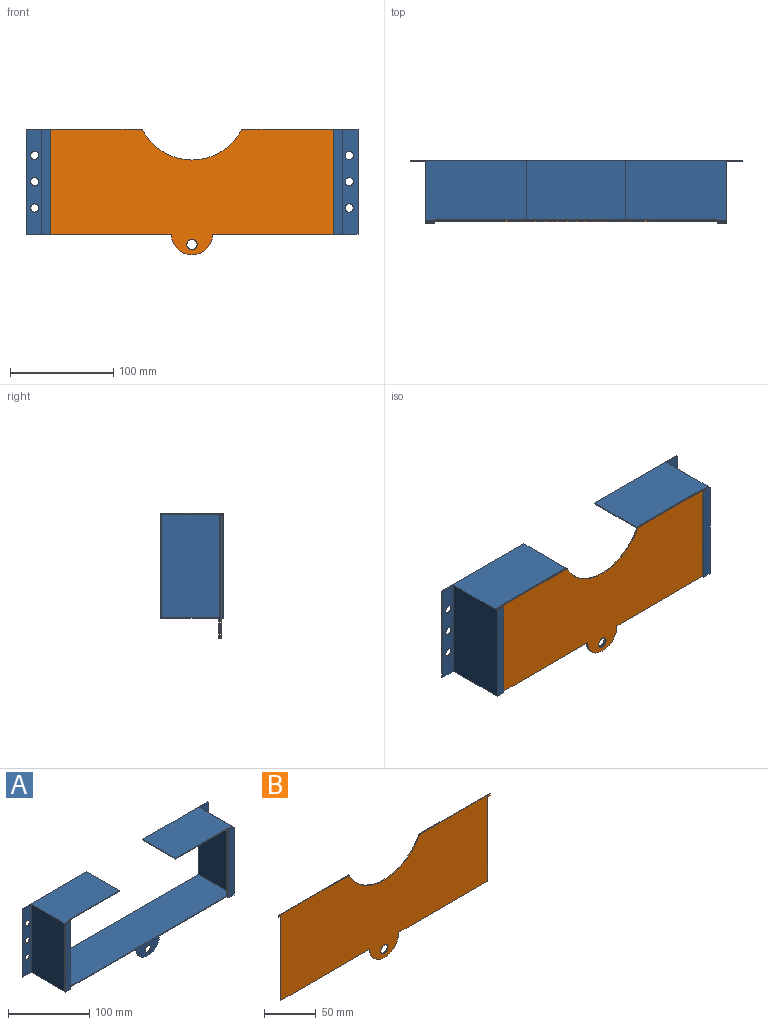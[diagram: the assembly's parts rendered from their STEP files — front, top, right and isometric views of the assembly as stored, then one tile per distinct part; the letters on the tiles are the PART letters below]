
ASSEMBLY  parts=2 mates=1
PART A: 47 faces, bbox 322x61x122 mm
  f0: plane 102x8mm, normal (0,1,0), area 813mm2, adj f4,f5,f12,f13,f42,f43
  f1: plane 100x57.5mm, normal (1,0,0), area 5750mm2, adj f8,f9,f33,f45
  f2: plane 102x60mm, normal (-1,0,0), area 6120mm2, adj f3,f11,f12,f13
  f3: plane 102x9mm, normal (0,-1,0), area 918mm2, adj f2,f4,f12,f13
  f4: plane 102x1mm, normal (1,0,0), area 102mm2, adj f0,f3,f12,f13
  f5: plane 101x1.5mm, normal (1,0,0), area 151.5mm2, adj f0,f6,f12,f43
  f6: plane 102x8mm, normal (0,-1,0), area 813mm2, adj f5,f7,f12,f13,f42,f43
  f7: plane 102x1mm, normal (1,0,0), area 102mm2, adj f6,f8,f12,f13,f17,f44
  f8: plane 100x8mm, normal (0,1,0), area 800mm2, adj f1,f7,f33,f45
  f9: plane 322x102mm, normal (0,1,0), area 3445.6mm2, adj f1,f10,f12,f13,f14,f15,f16,f21
  f10: plane 102x1mm, normal (-1,0,0), area 102mm2, adj f9,f11,f12,f13
  f11: plane 102x15mm, normal (0,-1,0), area 1379.2mm2, adj f2,f10,f12,f13,f14,f15,f16
  f12: plane 112.57x61mm, normal (0,0,1), area 5645mm2, adj f0,f2,f3,f4,f5,f6,f7,f9
  f13: plane 322x61mm, normal (0,0,-1), area 16828mm2, adj f0,f2,f3,f4,f6,f7,f9,f10
  f14: cylinder r=4mm len=8mm, axis (0,1,0), area 25.1mm2, adj f9,f11
  f15: cylinder r=4mm len=8mm, axis (0,1,0), area 25.1mm2, adj f9,f11
  f16: cylinder r=4mm len=8mm, axis (0,1,0), area 25.1mm2, adj f9,f11
  f17: plane 274x21mm, normal (0,-1,0), area 823.8mm2, adj f7,f13,f24,f33,f34,f35
  f18: plane 100x8mm, normal (0,1,0), area 800mm2, adj f21,f24,f33,f40
  f19: plane 102x8mm, normal (0,-1,0), area 813mm2, adj f13,f20,f24,f29,f37,f38
  f20: plane 101x1.5mm, normal (-1,0,0), area 151.5mm2, adj f19,f25,f29,f38
  f21: plane 100x57.5mm, normal (-1,0,0), area 5750mm2, adj f9,f18,f33,f40
  f22: plane 102x15mm, normal (0,-1,0), area 1379.2mm2, adj f13,f23,f28,f29,f30,f31,f32
  f23: plane 102x1mm, normal (1,0,0), area 102mm2, adj f9,f13,f22,f29
  f24: plane 102x1mm, normal (-1,0,0), area 102mm2, adj f13,f17,f18,f19,f29,f39
  f25: plane 102x8mm, normal (0,1,0), area 813mm2, adj f13,f20,f26,f29,f37,f38
  f26: plane 102x1mm, normal (-1,0,0), area 102mm2, adj f13,f25,f27,f29
  f27: plane 102x9mm, normal (0,-1,0), area 918mm2, adj f13,f26,f28,f29
  f28: plane 102x60mm, normal (1,0,0), area 6120mm2, adj f13,f22,f27,f29
  f29: plane 112.62x61mm, normal (0,0,1), area 5647.4mm2, adj f9,f19,f20,f22,f23,f24,f25,f26
  f30: cylinder r=4mm len=8mm, axis (0,1,0), area 25.1mm2, adj f9,f22
  f31: cylinder r=4mm len=8mm, axis (0,1,0), area 25.1mm2, adj f9,f22
  f32: cylinder r=4mm len=8mm, axis (0,1,0), area 25.1mm2, adj f9,f22
  f33: plane 290x57.5mm, normal (0,0,1), area 16675mm2, adj f1,f8,f9,f17,f18,f21
  f34: cylinder r=5mm len=10mm, axis (0,-1,0), area 31.4mm2, adj f17,f36
  f35: cylinder r=20mm len=40mm, axis (0,-1,0), area 62.8mm2, adj f13,f17,f36
  f36: plane 40x20mm, normal (0,1,0), area 549.8mm2, adj f13,f34,f35
  f37: plane 1.5x1mm, normal (-1,0,0), area 1.5mm2, adj f13,f19,f25,f38
  f38: plane 3x1.5mm, normal (0,0,1), area 4.5mm2, adj f19,f20,f25,f37
  f39: plane 88.62x1mm, normal (0,-1,0), area 88.6mm2, adj f24,f29,f40,f41
  f40: plane 96.62x57.5mm, normal (0,0,-1), area 5555.4mm2, adj f9,f18,f21,f39,f41
  f41: plane 57.5x1mm, normal (-1,0,0), area 57.5mm2, adj f9,f29,f39,f40
  f42: plane 1.5x1mm, normal (1,0,0), area 1.5mm2, adj f0,f6,f13,f43
  f43: plane 3x1.5mm, normal (0,0,1), area 4.5mm2, adj f0,f5,f6,f42
  f44: plane 88.57x1mm, normal (0,-1,0), area 88.6mm2, adj f7,f12,f45,f46
  f45: plane 96.57x57.5mm, normal (0,0,-1), area 5553mm2, adj f1,f8,f9,f44,f46
  f46: plane 57.5x1mm, normal (1,0,0), area 57.5mm2, adj f9,f12,f44,f45
PART B: 15 faces, bbox 290x1x122 mm
  f0: plane 96.63x1mm, normal (0,0,1), area 96.6mm2, adj f2,f3,f8,f14
  f1: plane 96.63x1mm, normal (0,0,1), area 96.6mm2, adj f2,f3,f7,f14
  f2: plane 290x122mm, normal (0,-1,0), area 27453.3mm2, adj f0,f1,f4,f5,f6,f7,f8,f9
  f3: plane 290x122mm, normal (0,1,0), area 27453.3mm2, adj f0,f1,f4,f5,f6,f7,f8,f9
  f4: plane 122x1mm, normal (0,0,-1), area 122mm2, adj f2,f3,f5,f13
  f5: plane 100x1mm, normal (1,0,0), area 100mm2, adj f2,f3,f4,f6
  f6: plane 3x1mm, normal (0,0,-1), area 3mm2, adj f2,f3,f5,f7
  f7: plane 2x1mm, normal (1,0,0), area 2mm2, adj f1,f2,f3,f6
  f8: plane 2x1mm, normal (-1,0,0), area 2mm2, adj f0,f2,f3,f9
  f9: plane 3x1mm, normal (0,0,-1), area 3mm2, adj f2,f3,f8,f10
  f10: plane 100x1mm, normal (-1,0,0), area 100mm2, adj f2,f3,f9,f11
  f11: plane 122x1mm, normal (0,0,-1), area 122mm2, adj f2,f3,f10,f13
  f12: cylinder r=5mm len=10mm, axis (0,1,0), area 31.4mm2, adj f2,f3
  f13: cylinder r=20mm len=40mm, axis (0,1,0), area 62.8mm2, adj f2,f3,f4,f11
  f14: cylinder r=54mm len=96.75mm, axis (0,1,0), area 119.9mm2, adj f0,f1,f2,f3
PLACE A t=(5,-26.83,-39.83)mm fixed
PLACE B t=(5,-24.05,-39.83)mm
MATE slider B.f4 <-> A.f13  axis (0,0,-1) through (86,-24.55,-39.83)mm
